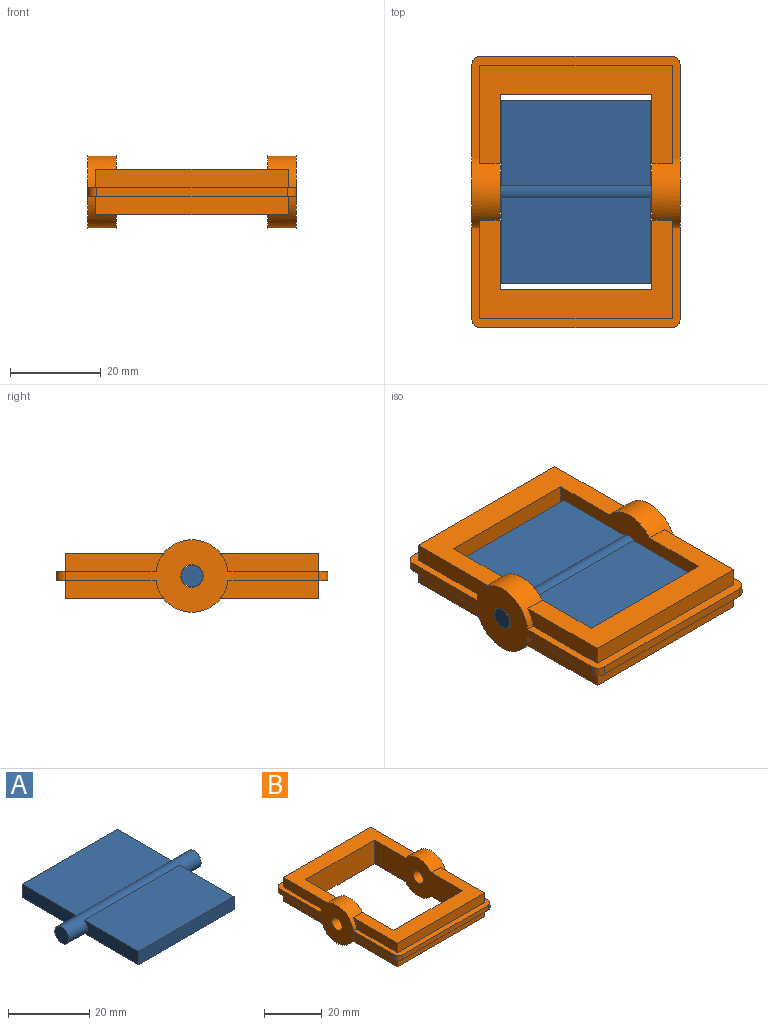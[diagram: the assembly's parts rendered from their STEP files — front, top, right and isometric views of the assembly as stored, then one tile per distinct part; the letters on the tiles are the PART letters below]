
ASSEMBLY  parts=2 mates=1
PART A: 13 faces, bbox 46x40.6x4.8 mm
  f0: plane 33.1x18.97mm, normal (0,0,-1), area 628mm2, adj f1,f2,f3,f5
  f1: plane 18.97x4mm, normal (1,0,0), area 72.9mm2, adj f0,f2,f4,f5
  f2: plane 33.1x4mm, normal (0,1,0), area 132.4mm2, adj f0,f1,f3,f4
  f3: plane 18.97x4mm, normal (-1,0,0), area 72.9mm2, adj f0,f2,f4,f5
  f4: plane 33.1x18.97mm, normal (0,0,1), area 628mm2, adj f1,f2,f3,f5
  f5: cylinder r=2.4mm len=46mm, axis (1,0,0), area 380.6mm2, adj f0,f1,f3,f4,f6,f7,f9,f10
  f6: plane 4.8x4.8mm, normal (-1,0,0), area 18.1mm2, adj f5
  f7: plane 4.8x4.8mm, normal (1,0,0), area 18.1mm2, adj f5
  f8: plane 33.1x4mm, normal (0,-1,0), area 132.4mm2, adj f9,f10,f11,f12
  f9: plane 33.1x18.97mm, normal (0,0,-1), area 628mm2, adj f5,f8,f11,f12
  f10: plane 33.1x18.97mm, normal (0,0,1), area 628mm2, adj f5,f8,f11,f12
  f11: plane 18.97x4mm, normal (-1,0,0), area 72.9mm2, adj f5,f8,f9,f10
  f12: plane 18.97x4mm, normal (1,0,0), area 72.9mm2, adj f5,f8,f9,f10
PART B: 38 faces, bbox 46x60x16 mm
  f0: plane 56x16mm, normal (-1,0,0), area 261.5mm2, adj f10,f12,f18,f23,f28,f29,f35,f36
  f1: cylinder r=8mm len=15.87mm, axis (1,0,0), area 104.5mm2, adj f4,f5,f6,f8,f12,f14,f22,f23
  f2: cylinder r=8mm len=15.87mm, axis (1,0,0), area 104.5mm2, adj f4,f5,f7,f9,f10,f15,f18,f27
  f3: cylinder r=2.5mm len=6.25mm, axis (1,0,0), area 98.2mm2, adj f4,f5
  f4: plane 43x16mm, normal (-1,0,0), area 462.6mm2, adj f1,f2,f3,f8,f9,f14,f15,f32
  f5: plane 56x16mm, normal (1,0,0), area 261.5mm2, adj f1,f2,f3,f10,f12,f18,f23,f30
  f6: plane 21.66x4mm, normal (1,0,0), area 82.4mm2, adj f1,f12,f14,f21
  f7: plane 21.66x4mm, normal (1,0,0), area 82.4mm2, adj f2,f15,f18,f24
  f8: plane 42.6x21.66mm, normal (0,0,1), area 411.5mm2, adj f1,f4,f11,f19,f22,f33,f34,f37
  f9: plane 42.6x21.66mm, normal (0,0,-1), area 411.5mm2, adj f2,f4,f13,f26,f27,f32,f33,f36
  f10: plane 46x22.06mm, normal (0,0,-1), area 162.8mm2, adj f0,f2,f5,f13,f16,f26,f27,f28
  f11: plane 21.66x4mm, normal (-1,0,0), area 82.4mm2, adj f8,f19,f23,f37
  f12: plane 46x22.06mm, normal (0,0,1), area 162.8mm2, adj f0,f1,f5,f6,f16,f20,f21,f28
  f13: plane 21.66x4mm, normal (-1,0,0), area 82.4mm2, adj f9,f10,f26,f36
  f14: plane 42.6x21.66mm, normal (0,0,1), area 411.5mm2, adj f1,f4,f6,f20,f21,f32,f33,f37
  f15: plane 42.6x21.66mm, normal (0,0,-1), area 411.5mm2, adj f2,f4,f7,f24,f25,f33,f34,f36
  f16: plane 42x2mm, normal (0,1,0), area 84mm2, adj f10,f12,f28,f31
  f17: plane 42x2mm, normal (0,-1,0), area 84mm2, adj f18,f23,f29,f30
  f18: plane 46x22.06mm, normal (0,0,-1), area 162.8mm2, adj f0,f2,f5,f7,f17,f24,f25,f29
  f19: plane 42.6x4mm, normal (0,-1,0), area 170.4mm2, adj f8,f11,f22,f23
  f20: plane 21.66x4mm, normal (-1,0,0), area 82.4mm2, adj f12,f14,f21,f37
  f21: plane 42.6x4mm, normal (0,1,0), area 170.4mm2, adj f6,f12,f14,f20
  f22: plane 21.66x4mm, normal (1,0,0), area 82.4mm2, adj f1,f8,f19,f23
  f23: plane 46x22.06mm, normal (0,0,1), area 162.8mm2, adj f0,f1,f5,f11,f17,f19,f22,f29
  f24: plane 42.6x4mm, normal (0,-1,0), area 170.4mm2, adj f7,f15,f18,f25
  f25: plane 21.66x4mm, normal (-1,0,0), area 82.4mm2, adj f15,f18,f24,f36
  f26: plane 42.6x4mm, normal (0,1,0), area 170.4mm2, adj f9,f10,f13,f27
  f27: plane 21.66x4mm, normal (1,0,0), area 82.4mm2, adj f2,f9,f10,f26
  f28: cylinder r=2mm len=2mm, axis (0,0,1), area 6.3mm2, adj f0,f10,f12,f16
  f29: cylinder r=2mm len=2mm, axis (0,0,-1), area 6.3mm2, adj f0,f17,f18,f23
  f30: cylinder r=2mm len=2mm, axis (0,0,-1), area 6.3mm2, adj f5,f17,f18,f23
  f31: cylinder r=2mm len=2mm, axis (0,0,1), area 6.3mm2, adj f5,f10,f12,f16
  f32: plane 33.5x10mm, normal (0,-1,0), area 335mm2, adj f4,f9,f14,f33
  f33: plane 43x16mm, normal (1,0,0), area 462.6mm2, adj f8,f9,f14,f15,f32,f34,f35,f36
  f34: plane 33.5x10mm, normal (0,1,0), area 335mm2, adj f4,f8,f15,f33
  f35: cylinder r=2.5mm len=6.25mm, axis (-1,0,0), area 98.2mm2, adj f0,f33
  f36: cylinder r=8mm len=15.87mm, axis (-1,0,0), area 104.5mm2, adj f0,f9,f10,f13,f15,f18,f25,f33
  f37: cylinder r=8mm len=15.87mm, axis (-1,0,0), area 104.5mm2, adj f0,f8,f11,f12,f14,f20,f23,f33
PLACE A t=(21.03,8.09,14.95)mm
PLACE B t=(21.03,8.09,14.95)mm
MATE revolute A.f5 <-> B.f35  axis (1,0,0) through (-19.58,8.09,15.95)mm
